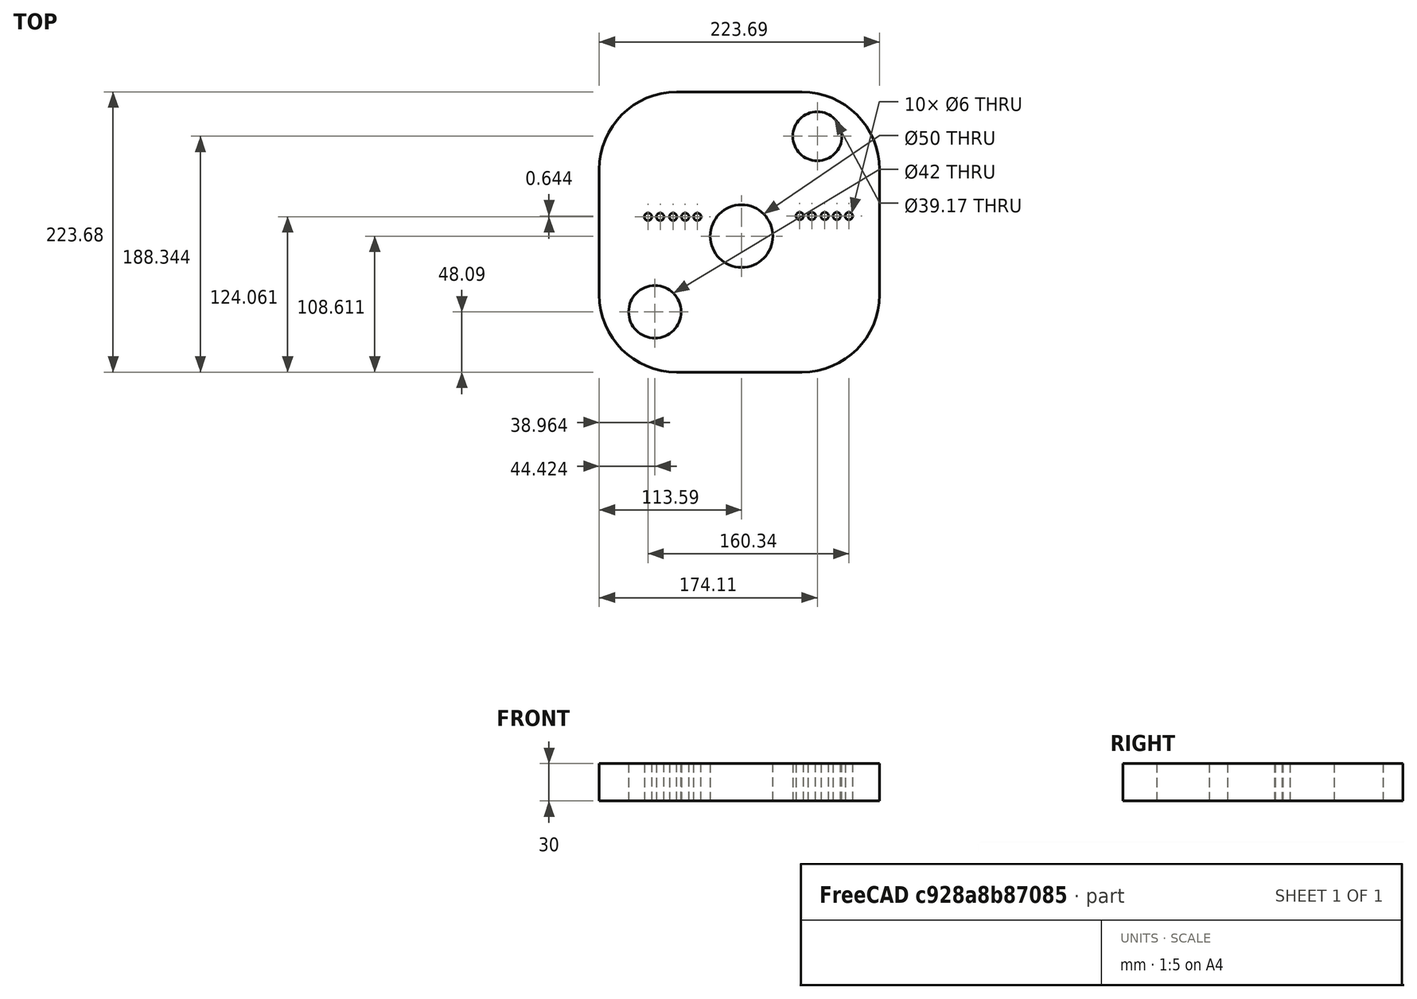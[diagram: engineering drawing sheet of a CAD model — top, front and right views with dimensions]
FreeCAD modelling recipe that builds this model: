
FCSTD DOCUMENT  (FreeCAD 0.18R16131 (Git))
Label: Momentum_Mold_Plate_1-2_160X200_12T_25mm(lm12uu) (3)
License: All rights reserved
LicenseURL: http://en.wikipedia.org/wiki/All_rights_reserved
objects: PartDesign::Pad×2, Sketcher::SketchObject×1, PartDesign::Body×1
note: 6 computed .brp shape members not serialized (recipe doc carries the construction recipe); baked Part::Feature solids carry a one-line shape summary decoded from their .brp

FEATURE [Sketcher::SketchObject] Sketch
  MapMode = 5
  Support = -> [XY_Plane]
  sketch-geometry (25):
    g0: LineSegment StartX=-51.695 StartY=-108.634 StartZ=0 EndX=48.305 EndY=-108.634 EndZ=0
    g1: LineSegment StartX=110.149 StartY=-46.7901 StartZ=0 EndX=110.149 EndY=53.2099 EndZ=0
    g2: LineSegment StartX=48.305 StartY=115.054 StartZ=0 EndX=-51.695 EndY=115.054 EndZ=0
    g3: LineSegment StartX=-113.539 StartY=53.2099 StartZ=0 EndX=-113.539 EndY=-46.7901 EndZ=0
    g4: Circle CenterX=0.050005 CenterY=-0.019529 CenterZ=0 NormalX=0 NormalY=0 NormalZ=1 AngleXU=0 Radius=25
    g5: Circle CenterX=-69.116 CenterY=-60.5398 CenterZ=0 NormalX=0 NormalY=0 NormalZ=1 AngleXU=0 Radius=21
    g6: Circle CenterX=60.5703 CenterY=79.7135 CenterZ=0 NormalX=0 NormalY=0 NormalZ=1 AngleXU=0 Radius=19.5845
    g7: ArcOfCircle CenterX=-51.695 CenterY=53.2099 CenterZ=0 NormalX=0 NormalY=0 NormalZ=1 AngleXU=0 Radius=61.844 StartAngle=1.5708 EndAngle=3.14159
    g8: ArcOfCircle CenterX=48.305 CenterY=53.2099 CenterZ=0 NormalX=0 NormalY=0 NormalZ=1 AngleXU=0 Radius=61.844 StartAngle=0 EndAngle=1.5708
    g9: ArcOfCircle CenterX=48.305 CenterY=-46.7901 CenterZ=0 NormalX=0 NormalY=0 NormalZ=1 AngleXU=0 Radius=61.844 StartAngle=4.71239 EndAngle=6.28319
    g10: ArcOfCircle CenterX=-51.695 CenterY=-46.7901 CenterZ=0 NormalX=0 NormalY=0 NormalZ=1 AngleXU=0 Radius=61.844 StartAngle=3.14159 EndAngle=4.71239
    g11: Circle CenterX=-74.5758 CenterY=15.4306 CenterZ=0 NormalX=0 NormalY=0 NormalZ=1 AngleXU=0 Radius=3
    g12: Circle CenterX=-64.9167 CenterY=15.4306 CenterZ=0 NormalX=0 NormalY=0 NormalZ=1 AngleXU=0 Radius=3
    g13: Circle CenterX=-54.6138 CenterY=15.4306 CenterZ=0 NormalX=0 NormalY=0 NormalZ=1 AngleXU=0 Radius=3
    g14: Circle CenterX=-44.9547 CenterY=15.4306 CenterZ=0 NormalX=0 NormalY=0 NormalZ=1 AngleXU=0 Radius=3
    g15: Circle CenterX=-35.2957 CenterY=15.4306 CenterZ=0 NormalX=0 NormalY=0 NormalZ=1 AngleXU=0 Radius=3
    g16: Circle CenterX=46.4841 CenterY=16.0746 CenterZ=0 NormalX=0 NormalY=0 NormalZ=1 AngleXU=0 Radius=3
    g17: Circle CenterX=56.1432 CenterY=16.0746 CenterZ=0 NormalX=0 NormalY=0 NormalZ=1 AngleXU=0 Radius=3
    g18: Circle CenterX=66.4461 CenterY=16.0746 CenterZ=0 NormalX=0 NormalY=0 NormalZ=1 AngleXU=0 Radius=3
    g19: Circle CenterX=76.1052 CenterY=16.0746 CenterZ=0 NormalX=0 NormalY=0 NormalZ=1 AngleXU=0 Radius=3
    g20: Circle CenterX=85.7642 CenterY=16.0746 CenterZ=0 NormalX=0 NormalY=0 NormalZ=1 AngleXU=0 Radius=3
    g21: Circle CenterX=-94.6859 CenterY=14.7421 CenterZ=0 NormalX=0 NormalY=0 NormalZ=1 AngleXU=0 Radius=3
    g22: Circle CenterX=-85.0268 CenterY=14.7421 CenterZ=0 NormalX=0 NormalY=0 NormalZ=1 AngleXU=0 Radius=3
    g23: Circle CenterX=36.0331 CenterY=15.386 CenterZ=0 NormalX=0 NormalY=0 NormalZ=1 AngleXU=0 Radius=3
    g24: Circle CenterX=95.2752 CenterY=15.386 CenterZ=0 NormalX=0 NormalY=0 NormalZ=1 AngleXU=0 Radius=3
  constraints (46):
    c: Horizontal(g0)
    c: Horizontal(g2)
    c: Vertical(g1)
    c: Vertical(g3)
    c: Radius(g4) = 25
    c: Radius(g5) = 21
    c: Tangent(g2,g7) = -1.5708
    c: Tangent(g3,g7) = -1.5708
    c: Tangent(g2,g8) = -1.5708
    c: Tangent(g1,g8) = -1.5708
    c: Tangent(g1,g9) = -1.5708
    c: Tangent(g0,g9) = -1.5708
    c: Tangent(g0,g10) = -1.5708
    c: Tangent(g3,g10) = -1.5708
    c: Vertical(g7,g10)
    c: DistanceY(g1,g1) = 100
    c: DistanceY(g3,g3) = 100
    c: Horizontal(g1,g3)
    c: DistanceX(g2,g2) = 100
    c: Horizontal(g11,g12)
    c: Horizontal(g12,g13)
    c: Horizontal(g13,g14)
    c: Horizontal(g14,g15)
    c: Horizontal(g16,g17)
    c: Horizontal(g17,g18)
    c: Horizontal(g18,g19)
    c: Horizontal(g19,g20)
    c: Horizontal(g21,g22)
    c: Horizontal(g21,g22)
    c: Horizontal(g22,g11)
    c: Horizontal(g11,g12)
    c: Horizontal(g12,g13)
    c: Horizontal(g13,g14)
    c: Horizontal(g14,g15)
    c: Equal(g21,g22)
    c: Equal(g22,g11)
    c: Equal(g11,g12)
    c: Equal(g12,g13)
    c: Equal(g13,g14)
    c: Equal(g14,g15)
    c: Horizontal(g18,g17)
    c: Horizontal(g17,g16)
    c: Horizontal(g16,g23)
    c: Horizontal(g23,g19)
    c: Horizontal(g19,g20)
    c: Horizontal(g20,g24)
FEATURE [PartDesign::Pad] Pad
  Length = 30
  Length2 = 100
  Profile = -> Sketch
  Type = 0
FEATURE [PartDesign::Pad] Pad001
  BaseFeature = -> Pad
  Length = 30
  Length2 = 100
  Profile = -> Sketch
  Type = 0
FEATURE [PartDesign::Body] Body
  Group = -> [Sketch,Pad,Pad001]
  Origin = -> Origin
  Tip = -> Pad001
